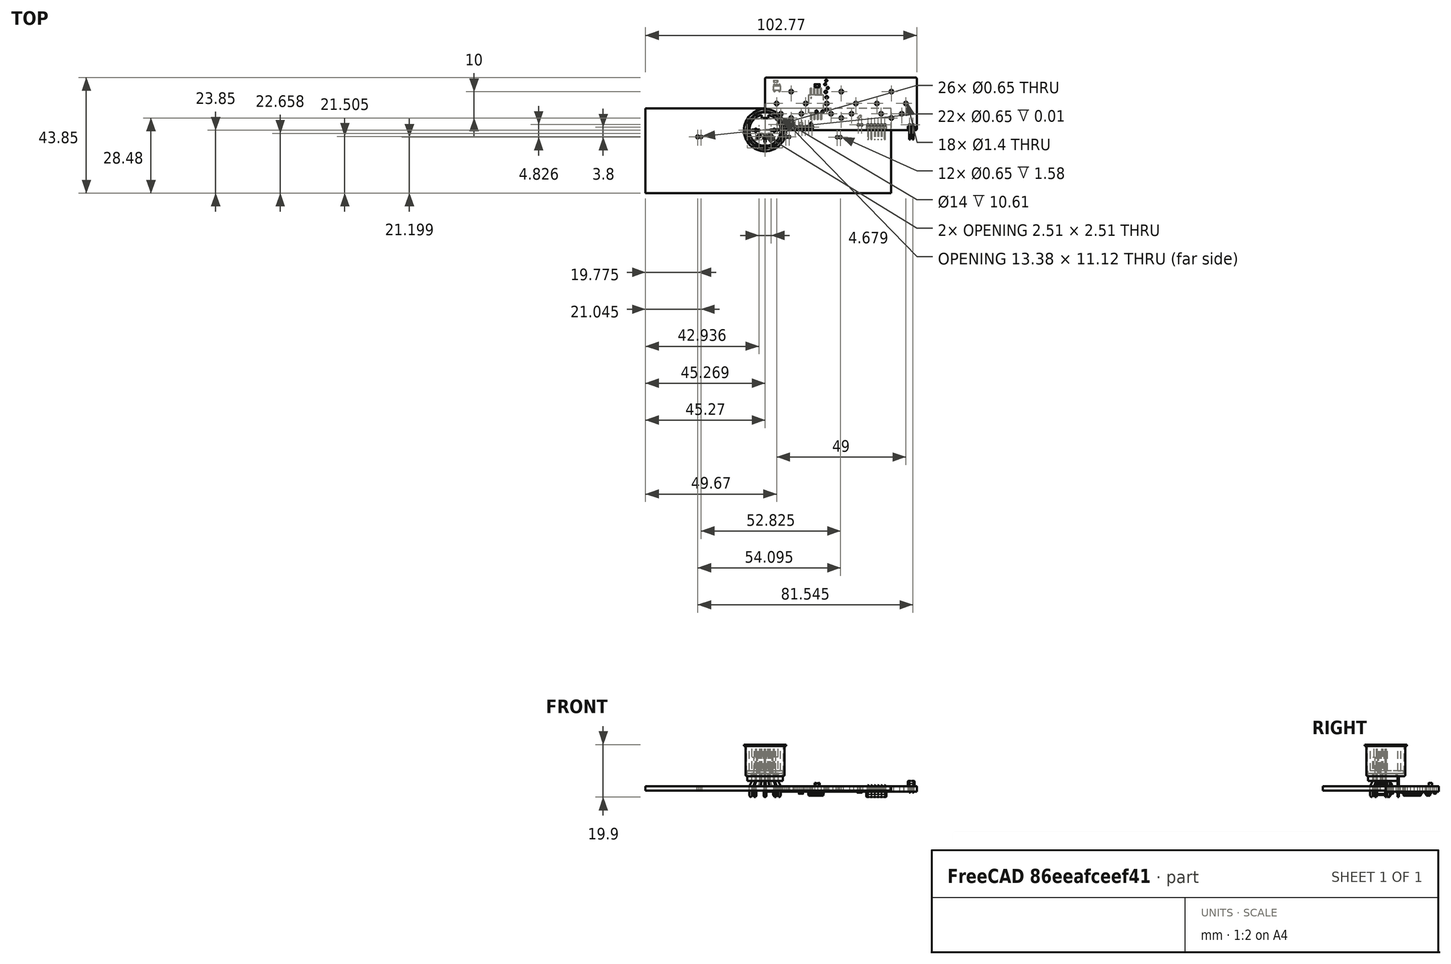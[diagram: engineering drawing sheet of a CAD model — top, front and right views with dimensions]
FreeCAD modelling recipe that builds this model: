
FCSTD DOCUMENT  (FreeCAD 0.20R29177 (Git))
Label: Ultra-midi
License: All rights reserved
LicenseURL: http://en.wikipedia.org/wiki/All_rights_reserved
objects: Part::Feature×33, App::Link×16, App::Part×8, Part::FeaturePython×5, App::DocumentObjectGroup×1, PartDesign::CoordinateSystem×1, Sketcher::SketchObject×1
note: 40 computed .brp shape members not serialized (recipe doc carries the construction recipe); baked Part::Feature solids carry a one-line shape summary decoded from their .brp

FEATURE [Part::FeaturePython] FCrtYd_lines  label="FCrtYd"  # a2plus imported part (geometry in sourceFile) (typed FeaturePython)
  Placement = pos=(0,0,0) rot=(0,0,1;1.5708rad)
  fixedPosition = true
FEATURE [Part::FeaturePython] FFab_lines  label="FFab"  # a2plus imported part (geometry in sourceFile) (typed FeaturePython)
  Placement = pos=(0,0,0) rot=(0,0,1;1.5708rad)
  fixedPosition = true
FEATURE [Part::FeaturePython] FSilk_lines  label="FrontSilk"  # a2plus imported part (geometry in sourceFile) (typed FeaturePython)
  Placement = pos=(0,0,0) rot=(0,0,1;1.5708rad)
  fixedPosition = true
FEATURE [Part::FeaturePython] THPs  label="PTHs"  # a2plus imported part (geometry in sourceFile) (typed FeaturePython)
  Placement = pos=(0,0,0) rot=(0,0,1;1.5708rad)
  fixedPosition = true
FEATURE [Part::Feature] Shape001003  label="TopPads"
  Placement = pos=(0,0,0) rot=(0,0,1;1.5708rad)
  shape: bbox 55.1 x 4.8 x 0.01 mm, 51 faces, 12 solids (baked)
FEATURE [Part::Feature] Shape001004  label="BotPads"
  Placement = pos=(0,0,0) rot=(0,0,1;1.5708rad)
  shape: bbox 55.1 x 4.8 x 0.01 mm, 51 faces, 12 solids (baked)
FEATURE [Part::FeaturePython] newPCB  label="Pcb"  # a2plus imported part (geometry in sourceFile) (typed FeaturePython)
  Placement = pos=(0,0,0) rot=(0,0,1;1.5708rad)
  fixedPosition = true
FEATURE [App::DocumentObjectGroup] Ultra_MIDI_daughter_fp
  Group = -> [FCrtYd_lines,FFab_lines,FSilk_lines,Shape001003,Shape001004,THPs,newPCB]
FEATURE [App::Link] C5_C_0603_1608Metric_0867c8c5745e_ln_  label="C2_C_0603_1608Metric_22715801060e"
  LinkPlacement = pos=(10.8,8.2,-2) rot=(1,0,0;3.14159rad)
  LinkedObject = -> Shape003
  Placement = pos=(10.8,8.2,-2) rot=(1,0,0;3.14159rad)
FEATURE [App::Link] C5_C_0603_1608Metric_0867c8c5745e_ln_001  label="C1_C_0603_1608Metric_b41121d6c93c"
  LinkPlacement = pos=(46.1,16.3,-2) rot=(0.92388,0.382683,0;3.14159rad)
  LinkedObject = -> Shape003
  Placement = pos=(46.1,16.3,-2) rot=(0.92388,0.382683,0;3.14159rad)
FEATURE [App::Link] C5_C_0603_1608Metric_0867c8c5745e_ln_002  label="C3_C_0603_1608Metric_cf41ac51516b"
  LinkPlacement = pos=(33.1375,16.2,-2) rot=(1,0,0;3.14159rad)
  LinkedObject = -> Shape003
  Placement = pos=(33.1375,16.2,-2) rot=(1,0,0;3.14159rad)
FEATURE [App::Link] C6_C_0805_2012Metric_c09b5ff471bc_ln_  label="C4_C_0805_2012Metric_26a949b8cd84"
  LinkPlacement = pos=(7,12.5,-2) rot=(0,1,0;3.14159rad)
  LinkedObject = -> Shape001
  Placement = pos=(7,12.5,-2) rot=(0,1,0;3.14159rad)
FEATURE [App::Link] FB3_L_0603_1608Metric_df2c29076625_ln_  label="FB1_L_0603_1608Metric_149065dd4c7b"
  LinkPlacement = pos=(36,7.4,-2) rot=(0.92388,0.382683,0;3.14159rad)
  LinkedObject = -> Shape002
  Placement = pos=(36,7.4,-2) rot=(0.92388,0.382683,0;3.14159rad)
FEATURE [App::Link] FB3_L_0603_1608Metric_df2c29076625_ln_001  label="FB2_L_0603_1608Metric_fe7989b07d85"
  LinkPlacement = pos=(12.8,12.2,-2) rot=(0.707107,0.707107,0;3.14159rad)
  LinkedObject = -> Shape002
  Placement = pos=(12.8,12.2,-2) rot=(0.707107,0.707107,0;3.14159rad)
FEATURE [App::Link] FB3_L_0603_1608Metric_df2c29076625_ln_002  label="FB4_L_0603_1608Metric_f99d6db0d256"
  LinkPlacement = pos=(54.15,6.2,-2) rot=(0.707107,-0.707107,0;3.14159rad)
  LinkedObject = -> Shape002
  Placement = pos=(54.15,6.2,-2) rot=(0.707107,-0.707107,0;3.14159rad)
FEATURE [App::Link] FB3_L_0603_1608Metric_df2c29076625_ln_003  label="FB5_L_0603_1608Metric_030844127197"
  LinkPlacement = pos=(25,3.4,-2) rot=(0,1,0;3.14159rad)
  LinkedObject = -> Shape002
  Placement = pos=(25,3.4,-2) rot=(0,1,0;3.14159rad)
FEATURE [App::Link] J2_PinHeader_1x02_P127mm_Horizontal_337eb045ee12_ln_  label="J3_PinHeader_1x02_P127mm_Horizontal_27ee44c8c3d4"
  LinkPlacement = pos=(36.65,2.025,0) rot=(0,0,-1;1.5708rad)
  LinkedObject = -> Shape
  Placement = pos=(36.65,2.025,0) rot=(0,0,-1;1.5708rad)
FEATURE [App::Link] J2_PinHeader_1x02_P127mm_Horizontal_337eb045ee12_ln_001  label="J1_PinHeader_1x02_P127mm_Horizontal_ae3b6cd6d5c1"
  LinkPlacement = pos=(4.6,2.175,-2) rot=(0.707107,-0.707107,0;3.14159rad)
  LinkedObject = -> Shape
  Placement = pos=(4.6,2.175,-2) rot=(0.707107,-0.707107,0;3.14159rad)
FEATURE [PartDesign::CoordinateSystem] Local_CS_69dd
  AttacherType = Attacher::AttachEngine3D
FEATURE [Sketcher::SketchObject] PCB_Sketch_69dd
  FullyConstrained = false
  sketch-geometry (18):
    g0: LineSegment StartX=57 StartY=20 StartZ=0 EndX=0.5 EndY=20 EndZ=0
    g1: LineSegment StartX=8e-16 StartY=19.5 StartZ=0 EndX=0 EndY=0.5 EndZ=0
    g2: LineSegment StartX=57.5 StartY=0.5 StartZ=0 EndX=57.5 EndY=19.5 EndZ=0
    g3: LineSegment StartX=0.5 StartY=0 StartZ=0 EndX=57 EndY=-1.3e-15 EndZ=0
    g4: ArcOfCircle CenterX=57 CenterY=0.500001 CenterZ=0 NormalX=0 NormalY=0 NormalZ=-1 AngleXU=-3.14159 Radius=0.500001 StartAngle=0 EndAngle=1.57079
    g5: ArcOfCircle CenterX=0.500001 CenterY=19.5 CenterZ=0 NormalX=0 NormalY=0 NormalZ=-1 AngleXU=2.66714e-06 Radius=0.500001 StartAngle=0 EndAngle=1.57079
    g6: ArcOfCircle CenterX=0.500001 CenterY=0.500001 CenterZ=0 NormalX=0 NormalY=0 NormalZ=-1 AngleXU=-1.57079 Radius=0.500001 StartAngle=0 EndAngle=1.57079
    g7: ArcOfCircle CenterX=57 CenterY=19.5 CenterZ=0 NormalX=0 NormalY=0 NormalZ=-1 AngleXU=1.5708 Radius=0.500001 StartAngle=0 EndAngle=1.57079
    g8: Circle CenterX=19.5 CenterY=7 CenterZ=0 NormalX=0 NormalY=0 NormalZ=1 AngleXU=0 Radius=0.5
    g9: Circle CenterX=17.4 CenterY=2.5 CenterZ=0 NormalX=0 NormalY=0 NormalZ=1 AngleXU=0 Radius=0.4
    g10: Circle CenterX=23.4 CenterY=7.8 CenterZ=0 NormalX=0 NormalY=0 NormalZ=1 AngleXU=0 Radius=0.5
    g11: Circle CenterX=23.2 CenterY=18.8 CenterZ=0 NormalX=0 NormalY=0 NormalZ=1 AngleXU=0 Radius=0.4
    g12: Circle CenterX=22.8 CenterY=17.4 CenterZ=0 NormalX=0 NormalY=0 NormalZ=1 AngleXU=0 Radius=0.4
    g13: Circle CenterX=23 CenterY=14.5 CenterZ=0 NormalX=0 NormalY=0 NormalZ=1 AngleXU=0 Radius=0.5
    g14: Circle CenterX=23.4 CenterY=12.5 CenterZ=0 NormalX=0 NormalY=0 NormalZ=1 AngleXU=0 Radius=0.5
    g15: Circle CenterX=17.4 CenterY=0.8 CenterZ=0 NormalX=0 NormalY=0 NormalZ=1 AngleXU=0 Radius=0.4
    g16: Circle CenterX=23.8 CenterY=16 CenterZ=0 NormalX=0 NormalY=0 NormalZ=1 AngleXU=0 Radius=0.4
    g17: Circle CenterX=21.8 CenterY=7 CenterZ=0 NormalX=0 NormalY=0 NormalZ=1 AngleXU=0 Radius=0.5
  constraints (8):
    c: Coincident(g1,g6)
    c: Coincident(g1,g5)
    c: Coincident(g3,g6)
    c: Coincident(g0,g5)
    c: Coincident(g3,g4)
    c: Coincident(g0,g7)
    c: Coincident(g2,g4)
    c: Coincident(g2,g7)
FEATURE [Part::Feature] Part__Feature  label="Casing"
  shape: bbox 18.09 x 18.09 x 19.8 mm, 30 faces (baked)
FEATURE [Part::Feature] Part__Feature001  label="Plastic"
  Placement = pos=(0,0,0) rot=(0,0,1;1.5708rad)
  shape: bbox 13.5 x 13.5 x 13.8 mm, 83 faces (baked)
FEATURE [Part::Feature] Part__Feature002  label="Pin-contact1"
  Placement = pos=(0,0,-4) rot=(0,0,1;0rad)
  shape: bbox 3.9 x 0.55 x 15 mm, 20 faces (baked)
FEATURE [Part::Feature] Part__Feature003  label="Pin-contact002"
  Placement = pos=(0,0,-4) rot=(0,0,1;1.5708rad)
  shape: bbox 0.55 x 3.9 x 15 mm, 20 faces (baked)
FEATURE [Part::Feature] Part__Feature004  label="Pin-contact003"
  Placement = pos=(0,0,-4) rot=(0,0,1;3.14159rad)
  shape: bbox 3.9 x 0.55 x 15 mm, 20 faces (baked)
FEATURE [Part::Feature] Part__Feature005  label="Pin-contact004"
  Placement = pos=(0,0,-4) rot=(0,0,1;0.785398rad)
  shape: bbox 3.147 x 3.147 x 15 mm, 20 faces (baked)
FEATURE [Part::Feature] Part__Feature006  label="Pin-contact005"
  Placement = pos=(0,0,-4) rot=(0,0,1;2.35619rad)
  shape: bbox 3.147 x 3.147 x 15 mm, 20 faces (baked)
FEATURE [App::Part] CUI_SD_50BV
  Group = -> [Part__Feature,Part__Feature001,Part__Feature002,Part__Feature003,Part__Feature004,Part__Feature005,Part__Feature006]
  Origin = -> Origin005
  Placement = pos=(9.9,10.15,0) rot=(0,0,1;0rad)
FEATURE [Part::Feature] Part__Feature007  label="Casing001"
  shape: bbox 18.09 x 18.09 x 19.8 mm, 30 faces (baked)
FEATURE [Part::Feature] Part__Feature008  label="Plastic001"
  Placement = pos=(0,0,0) rot=(0,0,1;1.5708rad)
  shape: bbox 13.5 x 13.5 x 13.8 mm, 83 faces (baked)
FEATURE [Part::Feature] Part__Feature009  label="Pin-contact006"
  Placement = pos=(0,0,-4) rot=(0,0,1;0rad)
  shape: bbox 3.9 x 0.55 x 15 mm, 20 faces (baked)
FEATURE [Part::Feature] Part__Feature010  label="Pin-contact007"
  Placement = pos=(0,0,-4) rot=(0,0,1;1.5708rad)
  shape: bbox 0.55 x 3.9 x 15 mm, 20 faces (baked)
FEATURE [Part::Feature] Part__Feature011  label="Pin-contact008"
  Placement = pos=(0,0,-4) rot=(0,0,1;3.14159rad)
  shape: bbox 3.9 x 0.55 x 15 mm, 20 faces (baked)
FEATURE [Part::Feature] Part__Feature012  label="Pin-contact009"
  Placement = pos=(0,0,-4) rot=(0,0,1;0.785398rad)
  shape: bbox 3.147 x 3.147 x 15 mm, 20 faces (baked)
FEATURE [Part::Feature] Part__Feature013  label="Pin-contact010"
  Placement = pos=(0,0,-4) rot=(0,0,1;2.35619rad)
  shape: bbox 3.147 x 3.147 x 15 mm, 20 faces (baked)
FEATURE [App::Part] CUI_SD_50BV001
  Group = -> [Part__Feature007,Part__Feature008,Part__Feature009,Part__Feature010,Part__Feature011,Part__Feature012,Part__Feature013]
  Origin = -> Origin006
  Placement = pos=(28.9,10.15,0) rot=(0,0,1;0rad)
FEATURE [Part::Feature] Part__Feature014  label="Casing002"
  shape: bbox 18.09 x 18.09 x 19.8 mm, 30 faces (baked)
FEATURE [Part::Feature] Part__Feature015  label="Plastic002"
  Placement = pos=(0,0,0) rot=(0,0,1;1.5708rad)
  shape: bbox 13.5 x 13.5 x 13.8 mm, 83 faces (baked)
FEATURE [Part::Feature] Part__Feature016  label="Pin-contact011"
  Placement = pos=(0,0,-4) rot=(0,0,1;0rad)
  shape: bbox 3.9 x 0.55 x 15 mm, 20 faces (baked)
FEATURE [Part::Feature] Part__Feature017  label="Pin-contact012"
  Placement = pos=(0,0,-4) rot=(0,0,1;1.5708rad)
  shape: bbox 0.55 x 3.9 x 15 mm, 20 faces (baked)
FEATURE [Part::Feature] Part__Feature018  label="Pin-contact013"
  Placement = pos=(0,0,-4) rot=(0,0,1;3.14159rad)
  shape: bbox 3.9 x 0.55 x 15 mm, 20 faces (baked)
FEATURE [Part::Feature] Part__Feature019  label="Pin-contact014"
  Placement = pos=(0,0,-4) rot=(0,0,1;0.785398rad)
  shape: bbox 3.147 x 3.147 x 15 mm, 20 faces (baked)
FEATURE [Part::Feature] Part__Feature020  label="Pin-contact015"
  Placement = pos=(0,0,-4) rot=(0,0,1;2.35619rad)
  shape: bbox 3.147 x 3.147 x 15 mm, 20 faces (baked)
FEATURE [App::Part] CUI_SD_50BV002
  Group = -> [Part__Feature014,Part__Feature015,Part__Feature016,Part__Feature017,Part__Feature018,Part__Feature019,Part__Feature020]
  Origin = -> Origin007
  Placement = pos=(47.9,10.15,0) rot=(0,0,1;0rad)
FEATURE [Part::Feature] Pcb_69dd
  Placement = pos=(-116,98,0) rot=(0,0,1;0rad)
  shape: bbox 57.5 x 20 x 2 mm, 50 faces (baked)
FEATURE [App::Link] R5_R_0603_1608Metric_8c8bab43711c_ln_  label="R4_R_0603_1608Metric_3ff6b89587b2"
  LinkPlacement = pos=(8,10,-2) rot=(0.707107,0.707107,0;3.14159rad)
  LinkedObject = -> Shape004
  Placement = pos=(8,10,-2) rot=(0.707107,0.707107,0;3.14159rad)
FEATURE [App::Link] R5_R_0603_1608Metric_8c8bab43711c_ln_001  label="R2_R_0603_1608Metric_4e10fd813094"
  LinkPlacement = pos=(49.4,16.5,-2) rot=(0.92388,-0.382683,0;3.14159rad)
  LinkedObject = -> Shape004
  Placement = pos=(49.4,16.5,-2) rot=(0.92388,-0.382683,0;3.14159rad)
FEATURE [App::Link] R5_R_0603_1608Metric_8c8bab43711c_ln_002  label="R7_R_0603_1608Metric_dfa80113c302"
  LinkPlacement = pos=(27,1.8,-2) rot=(0,1,0;3.14159rad)
  LinkedObject = -> Shape004
  Placement = pos=(27,1.8,-2) rot=(0,1,0;3.14159rad)
FEATURE [App::Link] R5_R_0603_1608Metric_8c8bab43711c_ln_003  label="R3_R_0603_1608Metric_b0f0240fa3c2"
  LinkPlacement = pos=(14,14.8,-2) rot=(0,1,0;3.14159rad)
  LinkedObject = -> Shape004
  Placement = pos=(14,14.8,-2) rot=(0,1,0;3.14159rad)
FEATURE [App::Link] R5_R_0603_1608Metric_8c8bab43711c_ln_004  label="R6_R_0603_1608Metric_639142cc7455"
  LinkPlacement = pos=(33.2,14.6,-2) rot=(0,1,0;3.14159rad)
  LinkedObject = -> Shape004
  Placement = pos=(33.2,14.6,-2) rot=(0,1,0;3.14159rad)
FEATURE [App::Link] R5_R_0603_1608Metric_8c8bab43711c_ln_005  label="R1_R_0603_1608Metric_cbd55fb59e40"
  LinkPlacement = pos=(53.25,3,-2) rot=(0.707107,0.707107,0;3.14159rad)
  LinkedObject = -> Shape004
  Placement = pos=(53.25,3,-2) rot=(0.707107,0.707107,0;3.14159rad)
FEATURE [Part::Feature] Shape  label="J2_PinHeader_1x02_P127mm_Horizontal_337eb045ee12"
  Placement = pos=(56.05,2.025,0) rot=(0,0,-1;1.5708rad)
  shape: bbox 2.54 x 5.7 x 4.5 mm, 58 faces (baked)
FEATURE [Part::Feature] Shape001  label="C6_C_0805_2012Metric_c09b5ff471bc"
  Placement = pos=(19.75,16.85,0) rot=(0,0,1;0rad)
  shape: bbox 2 x 1.25 x 1.25 mm, 28 faces (baked)
FEATURE [Part::Feature] Shape002  label="FB3_L_0603_1608Metric_df2c29076625"
  Placement = pos=(13.6,2.4,-2) rot=(0,1,0;3.14159rad)
  shape: bbox 1.6 x 0.8 x 0.8 mm, 28 faces (baked)
FEATURE [Part::Feature] Shape003  label="C5_C_0603_1608Metric_0867c8c5745e"
  Placement = pos=(4,18.6,-2) rot=(1,0,0;3.14159rad)
  shape: bbox 1.6 x 0.8 x 0.8 mm, 28 faces (baked)
FEATURE [Part::Feature] Shape004  label="R5_R_0603_1608Metric_8c8bab43711c"
  Placement = pos=(35.8,5,-2) rot=(0.92388,0.382683,0;3.14159rad)
  shape: bbox 1.697 x 1.697 x 0.45 mm, 26 faces (baked)
FEATURE [Part::Feature] Shape005  label="J4_PinHeader_1x06_P127mm_Horizontal_489f8f595e1f"
  Placement = pos=(39.025,2.025,-2) rot=(0.707107,-0.707107,0;3.14159rad)
  shape: bbox 7.62 x 5.7 x 4.5 mm, 166 faces (baked)
FEATURE [Part::Feature] Shape006  label="U1_SSO_8_68x59mm_P127mm_Clearance8mm_cd01ce0f9bbe"
  Placement = pos=(19.3,10,-2) rot=(0.707107,-0.707107,0;3.14159rad)
  shape: bbox 5.9 x 11.7 x 1.6 mm, 156 faces (baked)
FEATURE [Part::Feature] Shape007  label="U2_SOT_23_5_2942c334eb8a"
  Placement = pos=(4.5,16,-2) rot=(0.707107,-0.707107,0;3.14159rad)
  shape: bbox 2.9 x 2.8 x 1.55 mm, 109 faces (baked)
FEATURE [App::Part] Bot_69dd
  Group = -> [Shape002,Shape003,Shape004,Shape005,FB3_L_0603_1608Metric_df2c29076625_ln_,Shape006,Shape007,R5_R_0603_1608Metric_8c8bab43711c_ln_,C5_C_0603_1608Metric_0867c8c5745e_ln_,C6_C_0805_2012Metric_c09b5ff471bc_ln_,R5_R_0603_1608Metric_8c8bab43711c_ln_001,FB3_L_0603_1608Metric_df2c29076625_ln_001,C5_C_0603_1608Metric_0867c8c5745e_ln_001,R5_R_0603_1608Metric_8c8bab43711c_ln_002,+7 more]
  Origin = -> Origin004
FEATURE [App::Part] Top_69dd
  Group = -> [Shape,Shape001,J2_PinHeader_1x02_P127mm_Horizontal_337eb045ee12_ln_,CUI_SD_50BV,CUI_SD_50BV001,CUI_SD_50BV002]
  Origin = -> Origin003
FEATURE [App::Part] Step_Models_69dd
  Group = -> [Top_69dd,Bot_69dd]
  Origin = -> Origin002
FEATURE [Part::Feature] pads_area009001  label="topPads_69dd"
  Placement = pos=(-116,98,0.02) rot=(0,0,1;0rad)
  shape: bbox 54.45 x 16.58 x 2e-07 mm, 46 faces, 0 solids (baked)
FEATURE [App::Part] Board_Geoms_69dd
  Group = -> [Local_CS_69dd,Pcb_69dd,PCB_Sketch_69dd,pads_area009001]
  Origin = -> Origin
FEATURE [App::Part] Board_69dd  label="Ultra-Midi"
  Group = -> [Board_Geoms_69dd,Step_Models_69dd]
  Origin = -> Origin001
  Placement = pos=(-27.5,-1.5,0) rot=(1,0,0;1.5708rad)
